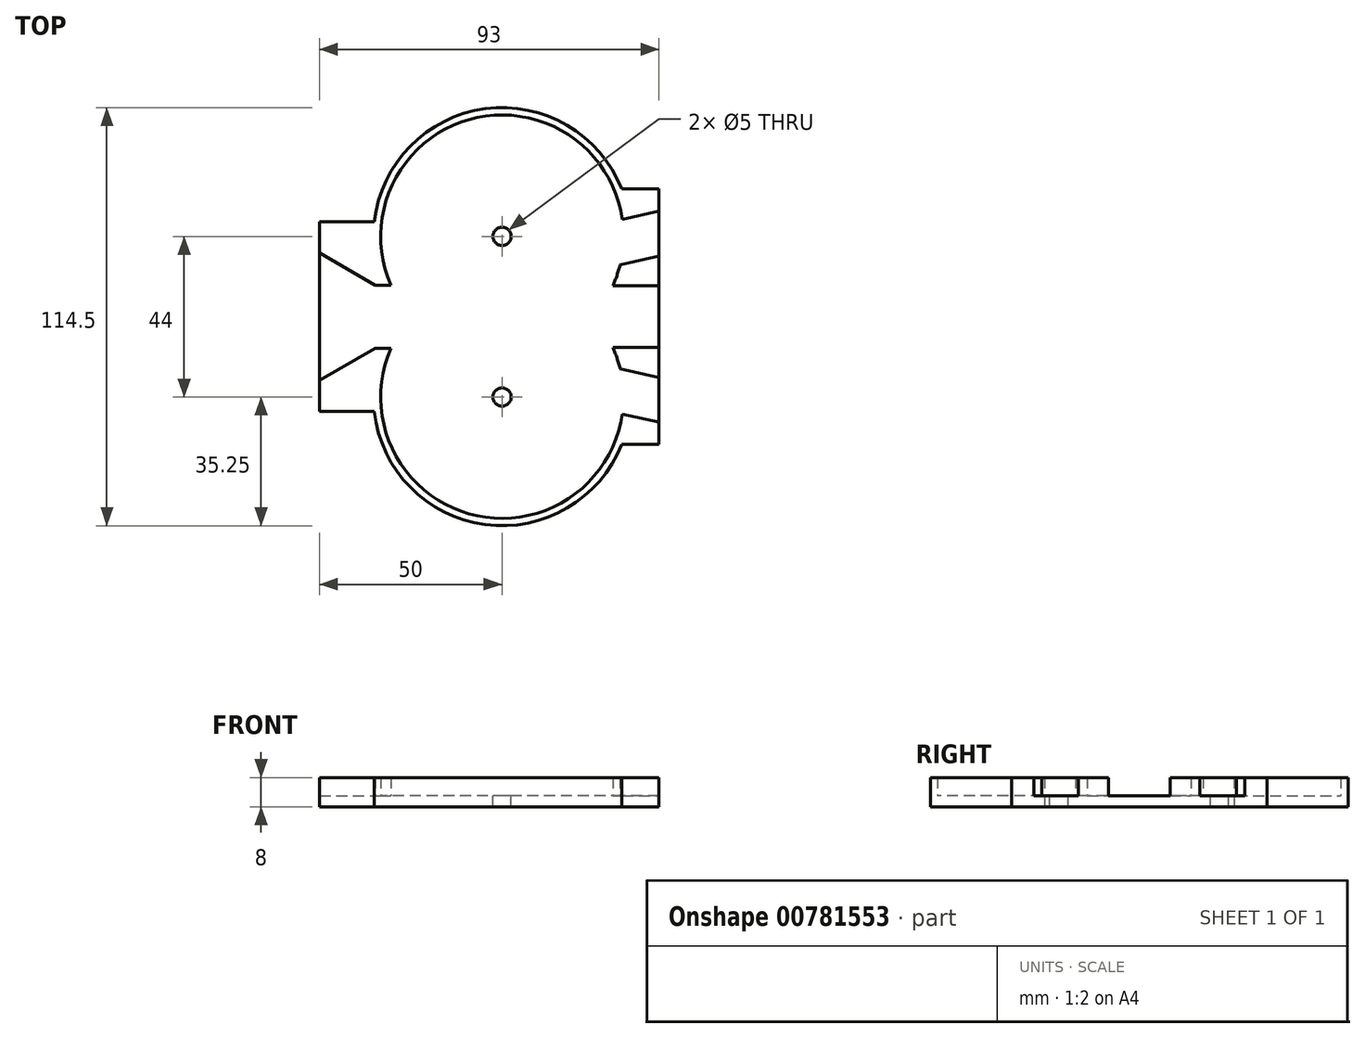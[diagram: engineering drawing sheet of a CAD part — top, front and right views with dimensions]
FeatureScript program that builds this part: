
annotation { "Feature Type Name" : "Feature", "Feature Type Description" : "" }
export const myFeature = defineFeature(function(context is Context, id is Id, definition is map)
    precondition{}
    {
        {
            var Q0;
            Q0=qCreatedBy(makeId("Top.planeOp"),FACE);
            var sketch = newSketch(context, id + "F0", { "sketchPlane" : qUnion([Q0])});
            skLineSegment(sketch, "E0.0.0", {"start": v(43, 35) * mm, "end": v(43, -35) * mm});
            skLineSegment(sketch, "E0.0.1", {"start": v(43, -35) * mm, "end": v(32.77, -35) * mm});
            skArc(sketch, "E0.0.2", {"start": v(32.77, -35) * mm, "mid": v(-4.64, -56.94) * mm, "end": v(-35.02, -26) * mm});
            skLineSegment(sketch, "E0.0.3", {"start": v(-35.02, -26) * mm, "end": v(-50, -26) * mm});
            skLineSegment(sketch, "E0.0.4", {"start": v(-50, -26) * mm, "end": v(-50, 26) * mm});
            skLineSegment(sketch, "E0.0.5", {"start": v(-50, 26) * mm, "end": v(-35.02, 26) * mm});
            skArc(sketch, "E0.0.6", {"start": v(-35.02, 26) * mm, "mid": v(-4.64, 56.94) * mm, "end": v(32.77, 35) * mm});
            skLineSegment(sketch, "E0.0.7", {"start": v(32.77, 35) * mm, "end": v(43, 35) * mm});
            skLineSegment(sketch, "E1", {"start": v(0, 22) * mm, "end": v(0, -22) * mm, "construction": true});
            skLineSegment(sketch, "E2", {"start": v(-50, 0) * mm, "end": v(43, 0) * mm, "construction": true});
            skSolve(sketch);
        }
        {
            var Q0;
            Q0 = qSketchRegion(id + "F0", true);
            extrude(context, id + "F1", {"entities" : qUnion([Q0]), "depth" : 3 * mm, "offsetDistance" : 25 * mm});
        }
        {
            var Q0;
            Q0=makeQuery(id+"F1.opExtrude","CAP_FACE",FACE,{"disambiguationData":[OSD([sQuery(id+"F0.wireOp",EDGE,"E0.0.0"),sQuery(id+"F0.wireOp",EDGE,"E0.0.1"),sQuery(id+"F0.wireOp",EDGE,"E0.0.2"),sQuery(id+"F0.wireOp",EDGE,"E0.0.3"),sQuery(id+"F0.wireOp",EDGE,"E0.0.4"),sQuery(id+"F0.wireOp",EDGE,"E0.0.5"),sQuery(id+"F0.wireOp",EDGE,"E0.0.6"),sQuery(id+"F0.wireOp",EDGE,"E0.0.7")])],"isStart":false});
            var sketch = newSketch(context, id + "F2", { "sketchPlane" : qUnion([Q0])});
            skArc(sketch, "E3.0.0", {"start": v(-30.46, 8.66) * mm, "mid": v(-9.08, 53.99) * mm, "end": v(32.92, 26.65) * mm});
            skLineSegment(sketch, "E3.0.1", {"start": v(32.92, 26.65) * mm, "end": v(43, 28.91) * mm});
            skLineSegment(sketch, "E3.0.2", {"start": v(43, 28.91) * mm, "end": v(43, 35) * mm});
            skLineSegment(sketch, "E3.0.3", {"start": v(43, 35) * mm, "end": v(32.77, 35) * mm});
            skArc(sketch, "E3.0.4", {"start": v(32.77, 35) * mm, "mid": v(-4.64, 56.94) * mm, "end": v(-35.02, 26) * mm});
            skLineSegment(sketch, "E3.0.5", {"start": v(-35.02, 26) * mm, "end": v(-50, 26) * mm});
            skLineSegment(sketch, "E3.0.6", {"start": v(-50, 26) * mm, "end": v(-50, 17.48) * mm});
            skLineSegment(sketch, "E3.0.7", {"start": v(-50, 17.48) * mm, "end": v(-34.8, 8.66) * mm});
            skLineSegment(sketch, "E3.0.8", {"start": v(-34.8, 8.66) * mm, "end": v(-30.46, 8.66) * mm});
            skArc(sketch, "E4.0.0", {"start": v(32.92, -26.65) * mm, "mid": v(-9.08, -53.99) * mm, "end": v(-30.46, -8.66) * mm});
            skLineSegment(sketch, "E4.0.1", {"start": v(-30.46, -8.66) * mm, "end": v(-34.8, -8.66) * mm});
            skLineSegment(sketch, "E4.0.2", {"start": v(-34.8, -8.66) * mm, "end": v(-50, -17.48) * mm});
            skLineSegment(sketch, "E4.0.3", {"start": v(-50, -17.48) * mm, "end": v(-50, -26) * mm});
            skLineSegment(sketch, "E4.0.4", {"start": v(-50, -26) * mm, "end": v(-35.02, -26) * mm});
            skArc(sketch, "E4.0.5", {"start": v(-35.02, -26) * mm, "mid": v(-4.64, -56.94) * mm, "end": v(32.77, -35) * mm});
            skLineSegment(sketch, "E4.0.6", {"start": v(32.77, -35) * mm, "end": v(43, -35) * mm});
            skLineSegment(sketch, "E4.0.7", {"start": v(43, -35) * mm, "end": v(43, -28.91) * mm});
            skLineSegment(sketch, "E4.0.8", {"start": v(43, -28.91) * mm, "end": v(32.92, -26.65) * mm});
            skArc(sketch, "E5.0.0", {"start": v(32.33, 14.23) * mm, "mid": v(31.48, 11.29) * mm, "end": v(30.36, 8.43) * mm});
            skLineSegment(sketch, "E5.0.1", {"start": v(30.36, 8.43) * mm, "end": v(43, 8.43) * mm});
            skLineSegment(sketch, "E5.0.2", {"start": v(43, 8.43) * mm, "end": v(43, 16.63) * mm});
            skLineSegment(sketch, "E5.0.3", {"start": v(43, 16.63) * mm, "end": v(32.33, 14.23) * mm});
            skArc(sketch, "E6.0.0", {"start": v(30.36, -8.43) * mm, "mid": v(31.48, -11.29) * mm, "end": v(32.33, -14.23) * mm});
            skLineSegment(sketch, "E6.0.1", {"start": v(32.33, -14.23) * mm, "end": v(43, -16.63) * mm});
            skLineSegment(sketch, "E6.0.2", {"start": v(43, -16.63) * mm, "end": v(43, -8.43) * mm});
            skLineSegment(sketch, "E6.0.3", {"start": v(43, -8.43) * mm, "end": v(30.36, -8.43) * mm});
            skLineSegment(sketch, "E7", {"start": v(0, 22) * mm, "end": v(0, -22) * mm, "construction": true});
            skLineSegment(sketch, "E8", {"start": v(-30.46, 8.66) * mm, "end": v(0, 22) * mm, "construction": true});
            skLineSegment(sketch, "E9", {"start": v(0, 22) * mm, "end": v(43, 22) * mm, "construction": true});
            skLineSegment(sketch, "E10", {"start": v(-50, 0) * mm, "end": v(43, 0) * mm, "construction": true});
            skLineSegment(sketch, "E11", {"start": v(0, 22) * mm, "end": v(32.92, 26.65) * mm, "construction": true});
            skSolve(sketch);
        }
        {
            var Q0;
            Q0 = qSketchRegion(id + "F2", true);
            extrude(context, id + "F3", {"entities" : qUnion([Q0]), "operationType" : NewBodyOperationType.ADD, "depth" : 5 * mm, "offsetDistance" : 25 * mm});
        }
        {
            var Q0;
            Q0=makeQuery(id+"F1.opExtrude","CAP_FACE",FACE,{"disambiguationData":[OSD([sQuery(id+"F0.wireOp",EDGE,"E0.0.0"),sQuery(id+"F0.wireOp",EDGE,"E0.0.1"),sQuery(id+"F0.wireOp",EDGE,"E0.0.2"),sQuery(id+"F0.wireOp",EDGE,"E0.0.3"),sQuery(id+"F0.wireOp",EDGE,"E0.0.4"),sQuery(id+"F0.wireOp",EDGE,"E0.0.5"),sQuery(id+"F0.wireOp",EDGE,"E0.0.6"),sQuery(id+"F0.wireOp",EDGE,"E0.0.7")])],"isStart":false});
            var sketch = newSketch(context, id + "F4", { "sketchPlane" : qUnion([Q0])});
            skCircle(sketch, "E12", {"center": v(0, 22) * mm, "radius": 2.5 * mm});
            skCircle(sketch, "E13", {"center": v(0, -22) * mm, "radius": 2.5 * mm});
            skSolve(sketch);
        }
        {
            var Q0;
            Q0 = qSketchRegion(id + "F4", true);
            extrude(context, id + "F5", {"entities" : qUnion([Q0]), "operationType" : NewBodyOperationType.REMOVE, "endBound" : BoundingType.THROUGH_ALL, "oppositeDirection" : true, "depth" : 25 * mm, "offsetDistance" : 25 * mm});
        }
    });
